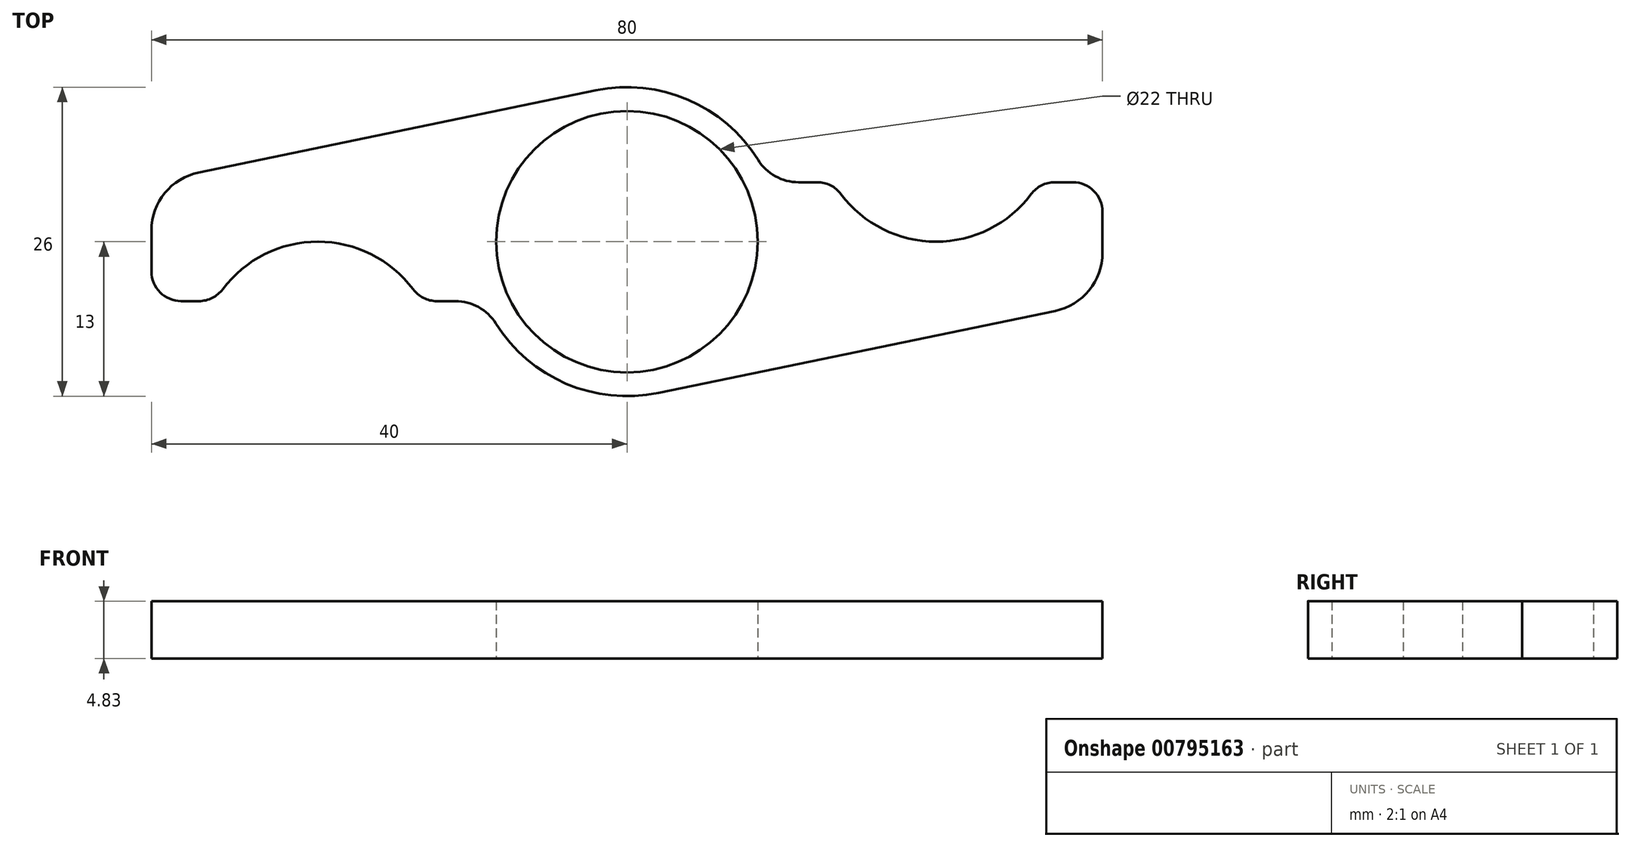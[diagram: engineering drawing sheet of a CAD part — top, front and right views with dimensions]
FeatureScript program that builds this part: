
annotation { "Feature Type Name" : "Feature", "Feature Type Description" : "" }
export const myFeature = defineFeature(function(context is Context, id is Id, definition is map)
    precondition{}
    {
        {
            var Q0;
            Q0=qCreatedBy(makeId("Top.planeOp"),FACE);
            var sketch = newSketch(context, id + "F0", { "sketchPlane" : qUnion([Q0])});
            skCircle(sketch, "E0", {"center": v(0, 0) * mm, "radius": 11 * mm});
            skArc(sketch, "E1", {"start": v(-11.03, -6.88) * mm, "mid": v(-5.12, -11.95) * mm, "end": v(2.63, -12.73) * mm});
            skLineSegment(sketch, "E2", {"start": v(-40, 0.93) * mm, "end": v(-40, -2.5) * mm});
            skCircle(sketch, "E3", {"center": v(0, 0) * mm, "radius": 50 * mm, "construction": true});
            skLineSegment(sketch, "E4", {"start": v(-36.01, 5.82) * mm, "end": v(-2.63, 12.73) * mm});
            skLineSegment(sketch, "E5", {"start": v(-37.5, -5) * mm, "end": v(-36, -5) * mm});
            skArc(sketch, "E6", {"start": v(-18, -4) * mm, "mid": v(-26, 0) * mm, "end": v(-34, -4) * mm});
            skLineSegment(sketch, "E7.trimOffspring", {"start": v(-16, -5) * mm, "end": v(-14.42, -5) * mm});
            skPoint(sketch, "E8.visualSharp", {"position": v(-40, 5) * mm});
            skArc(sketch, "E8.filletArc", {"start": v(-36.01, 5.82) * mm, "mid": v(-38.88, 4.09) * mm, "end": v(-40, 0.93) * mm});
            skPoint(sketch, "E9.visualSharp", {"position": v(-40, -5) * mm});
            skArc(sketch, "E9.filletArc", {"start": v(-40, -2.5) * mm, "mid": v(-39.27, -4.27) * mm, "end": v(-37.5, -5) * mm});
            skPoint(sketch, "E10.visualSharp", {"position": v(-34.66, -5) * mm});
            skArc(sketch, "E10.filletArc", {"start": v(-36, -5) * mm, "mid": v(-34.88, -4.74) * mm, "end": v(-34, -4) * mm});
            skPoint(sketch, "E11.visualSharp", {"position": v(-17.34, -5) * mm});
            skArc(sketch, "E11.filletArc", {"start": v(-18, -4) * mm, "mid": v(-17.12, -4.74) * mm, "end": v(-16, -5) * mm});
            skPoint(sketch, "E12.1.0", {"position": v(17.34, 5) * mm});
            skLineSegment(sketch, "E12.1.1", {"start": v(40, -0.93) * mm, "end": v(40, 2.5) * mm});
            skLineSegment(sketch, "E12.1.2", {"start": v(36.01, -5.82) * mm, "end": v(2.63, -12.73) * mm});
            skPoint(sketch, "E12.1.3", {"position": v(40, -5) * mm});
            skArc(sketch, "E12.1.4", {"start": v(18, 4) * mm, "mid": v(26, 0) * mm, "end": v(34, 4) * mm});
            skLineSegment(sketch, "E12.1.5", {"start": v(16, 5) * mm, "end": v(14.42, 5) * mm});
            skArc(sketch, "E12.1.6", {"start": v(36.01, -5.82) * mm, "mid": v(38.88, -4.09) * mm, "end": v(40, -0.93) * mm});
            skPoint(sketch, "E12.1.7", {"position": v(34.66, 5) * mm});
            skPoint(sketch, "E12.1.8", {"position": v(40, 5) * mm});
            skArc(sketch, "E12.1.9", {"start": v(40, 2.5) * mm, "mid": v(39.27, 4.27) * mm, "end": v(37.5, 5) * mm});
            skArc(sketch, "E12.1.10", {"start": v(36, 5) * mm, "mid": v(34.88, 4.74) * mm, "end": v(34, 4) * mm});
            skLineSegment(sketch, "E12.1.11", {"start": v(37.5, 5) * mm, "end": v(36, 5) * mm});
            skArc(sketch, "E12.1.12", {"start": v(18, 4) * mm, "mid": v(17.12, 4.74) * mm, "end": v(16, 5) * mm});
            skArc(sketch, "E13.trimOffspring", {"start": v(11.03, 6.88) * mm, "mid": v(5.12, 11.95) * mm, "end": v(-2.63, 12.73) * mm});
            skPoint(sketch, "E14.visualSharp", {"position": v(-12, -5) * mm});
            skArc(sketch, "E14.filletArc", {"start": v(-11.03, -6.88) * mm, "mid": v(-12.48, -5.5) * mm, "end": v(-14.42, -5) * mm});
            skPoint(sketch, "E15.visualSharp", {"position": v(12, 5) * mm});
            skArc(sketch, "E15.filletArc", {"start": v(11.03, 6.88) * mm, "mid": v(12.48, 5.5) * mm, "end": v(14.42, 5) * mm});
            skSolve(sketch);
        }
        {
            var Q0;
            Q0=makeQuery(id+"F0.imprint","IMPRINT",FACE,{"disambiguationData":[TD([[makeQuery(id+"F0.imprint","IMPRINT",EDGE,{"derivedFrom":sQuery(id+"F0.wireOp",EDGE,"E0")}),-1.0]])]});
            extrude(context, id + "F1", {"entities" : qUnion([Q0]), "depth" : 4.83 * mm, "offsetDistance" : 25 * mm});
        }
    });
